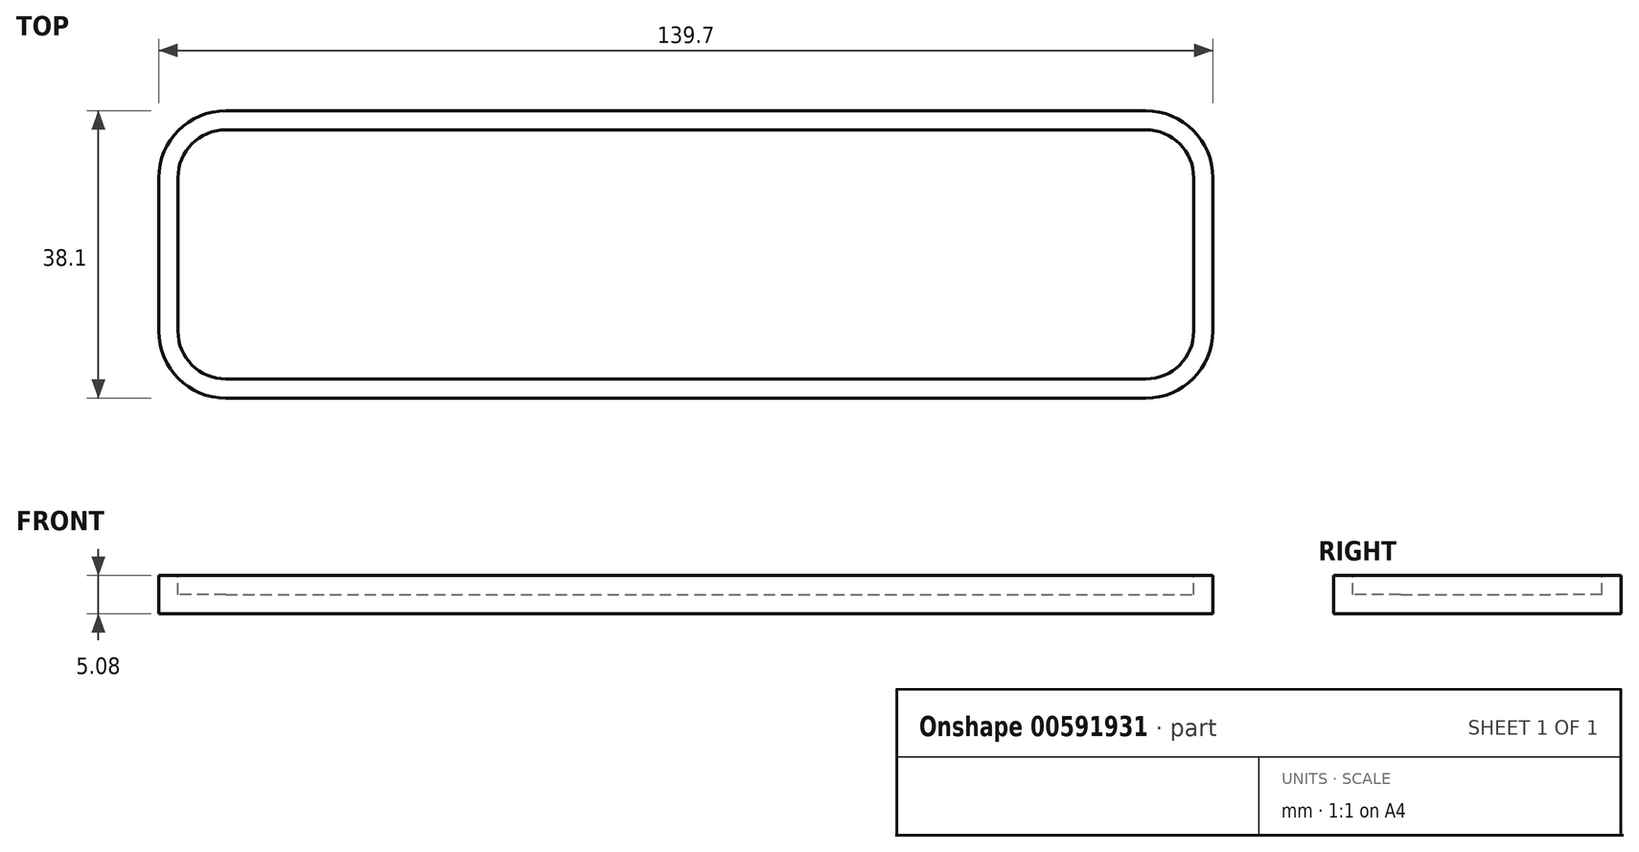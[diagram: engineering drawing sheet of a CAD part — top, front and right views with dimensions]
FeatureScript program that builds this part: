
annotation { "Feature Type Name" : "Feature", "Feature Type Description" : "" }
export const myFeature = defineFeature(function(context is Context, id is Id, definition is map)
    precondition{}
    {
        {
            var Q0;
            Q0=qCreatedBy(makeId("Top.planeOp"),FACE);
            var sketch = newSketch(context, id + "F0", { "sketchPlane" : qUnion([Q0])});
            skLineSegment(sketch, "E0.bottom", {"start": v(8.89, 0) * mm, "end": v(130.8, 0) * mm});
            skLineSegment(sketch, "E0.top", {"start": v(8.89, 38.1) * mm, "end": v(130.8, 38.1) * mm});
            skLineSegment(sketch, "E0.left", {"start": v(0, 8.89) * mm, "end": v(0, 29.21) * mm});
            skLineSegment(sketch, "E0.right", {"start": v(139.7, 8.9) * mm, "end": v(139.7, 29.21) * mm});
            skPoint(sketch, "E1.visualSharp", {"position": v(0, 38.1) * mm});
            skArc(sketch, "E1.filletArc", {"start": v(8.89, 38.1) * mm, "mid": v(2.6, 35.5) * mm, "end": v(0, 29.21) * mm});
            skPoint(sketch, "E2.visualSharp", {"position": v(139.7, 38.1) * mm});
            skArc(sketch, "E2.filletArc", {"start": v(139.7, 29.21) * mm, "mid": v(137.1, 35.5) * mm, "end": v(130.8, 38.1) * mm});
            skPoint(sketch, "E3.visualSharp", {"position": v(139.7, 0) * mm});
            skArc(sketch, "E3.filletArc", {"start": v(130.8, 0) * mm, "mid": v(137.1, 2.6) * mm, "end": v(139.7, 8.9) * mm});
            skPoint(sketch, "E4.visualSharp", {"position": v(0, 0) * mm});
            skArc(sketch, "E4.filletArc", {"start": v(0, 8.89) * mm, "mid": v(2.6, 2.6) * mm, "end": v(8.89, 0) * mm});
            skSolve(sketch);
        }
        {
            var Q0;
            Q0 = qSketchRegion(id + "F0", true);
            extrude(context, id + "F1", {"entities" : qUnion([Q0]), "depth" : 5.08 * mm, "offsetDistance" : 25.4 * mm});
        }
        {
            var Q0;
            Q0=makeQuery(id+"F1.opExtrude","CAP_FACE",FACE,{"disambiguationData":[OSD([sQuery(id+"F0.wireOp",EDGE,"E0.bottom"),sQuery(id+"F0.wireOp",EDGE,"E0.top"),sQuery(id+"F0.wireOp",EDGE,"E0.left"),sQuery(id+"F0.wireOp",EDGE,"E0.right"),sQuery(id+"F0.wireOp",EDGE,"E1.filletArc"),sQuery(id+"F0.wireOp",EDGE,"E2.filletArc"),sQuery(id+"F0.wireOp",EDGE,"E3.filletArc"),sQuery(id+"F0.wireOp",EDGE,"E4.filletArc")])],"isStart":false});
            var sketch = newSketch(context, id + "F2", { "sketchPlane" : qUnion([Q0])});
            skArc(sketch, "E5.0", {"start": v(8.89, 35.56) * mm, "mid": v(4.4, 33.7) * mm, "end": v(2.54, 29.21) * mm});
            skLineSegment(sketch, "E5.1", {"start": v(2.54, 8.9) * mm, "end": v(2.54, 29.21) * mm});
            skLineSegment(sketch, "E5.2", {"start": v(8.89, 35.56) * mm, "end": v(130.8, 35.56) * mm});
            skArc(sketch, "E5.3", {"start": v(2.54, 8.9) * mm, "mid": v(4.4, 4.4) * mm, "end": v(8.89, 2.54) * mm});
            skArc(sketch, "E5.4", {"start": v(137.16, 29.21) * mm, "mid": v(135.3, 33.7) * mm, "end": v(130.8, 35.56) * mm});
            skLineSegment(sketch, "E5.5", {"start": v(137.16, 8.9) * mm, "end": v(137.16, 29.21) * mm});
            skArc(sketch, "E5.6", {"start": v(130.8, 2.54) * mm, "mid": v(135.3, 4.4) * mm, "end": v(137.16, 8.9) * mm});
            skLineSegment(sketch, "E5.7", {"start": v(8.89, 2.54) * mm, "end": v(130.8, 2.54) * mm});
            skSolve(sketch);
        }
        {
            var Q0;
            Q0 = qSketchRegion(id + "F2", true);
            extrude(context, id + "F3", {"entities" : qUnion([Q0]), "operationType" : NewBodyOperationType.REMOVE, "oppositeDirection" : true, "depth" : 2.54 * mm, "offsetDistance" : 25.4 * mm});
        }
    });
